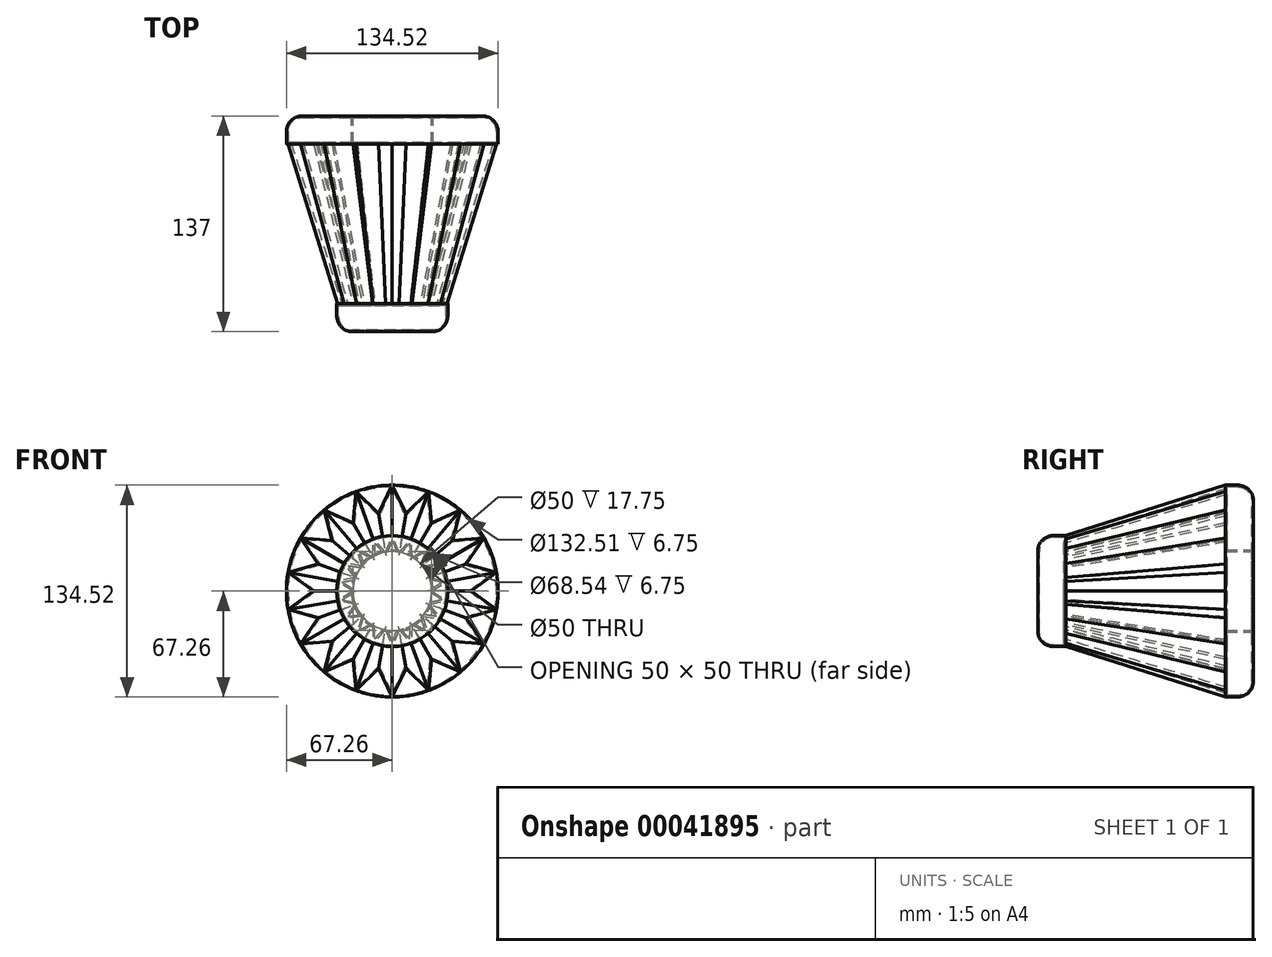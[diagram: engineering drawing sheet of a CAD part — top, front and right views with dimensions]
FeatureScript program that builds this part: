
annotation { "Feature Type Name" : "Feature", "Feature Type Description" : "" }
export const myFeature = defineFeature(function(context is Context, id is Id, definition is map)
    precondition{}
    {
        {
            var Q0;
            Q0=qCreatedBy(makeId("Front.planeOp"),FACE);
            var sketch = newSketch(context, id + "F0", { "sketchPlane" : qUnion([Q0])});
            skLineSegment(sketch, "E0", {"start": v(0, 0) * mm, "end": v(0, 67.26) * mm, "construction": true});
            skLineSegment(sketch, "E1", {"start": v(0, 0) * mm, "end": v(-8.68, 49.24) * mm});
            skLineSegment(sketch, "E2", {"start": v(-8.68, 49.24) * mm, "end": v(0, 67.26) * mm});
            skLineSegment(sketch, "E3.MirrorCS", {"start": v(8.68, 49.24) * mm, "end": v(0, 67.26) * mm});
            skLineSegment(sketch, "E4.MirrorCS", {"start": v(0, 0) * mm, "end": v(8.68, 49.24) * mm});
            skSolve(sketch);
        }
        {
            var Q0;
            Q0=qCreatedBy(makeId("Front.planeOp"),FACE);
            cPlane(context, id + "F1", {"entities" : qUnion([Q0]), "cplaneType" : CPlaneType.OFFSET, "offset" : 101.5 * mm, "width" : 150 * mm, "height" : 150 * mm});
        }
        {
            var Q0;
            Q0=qCreatedBy(id+"F1.planeOp",FACE);
            var sketch = newSketch(context, id + "F2", { "sketchPlane" : qUnion([Q0])});
            skLineSegment(sketch, "E5", {"start": v(0, 0) * mm, "end": v(0, 49.56) * mm, "construction": true});
            skLineSegment(sketch, "E6", {"start": v(0, 0) * mm, "end": v(-4.34, 24.62) * mm});
            skLineSegment(sketch, "E7", {"start": v(-4.34, 24.62) * mm, "end": v(0, 35.27) * mm});
            skLineSegment(sketch, "E8.MirrorCS", {"start": v(4.34, 24.62) * mm, "end": v(0, 35.27) * mm});
            skLineSegment(sketch, "E9.MirrorCS", {"start": v(0, 0) * mm, "end": v(4.34, 24.62) * mm});
            skSolve(sketch);
        }
        {
            var Q0;
            Q0=makeQuery(id+"F0.imprint","IMPRINT",FACE,{"disambiguationData":[TD([[makeQuery(id+"F0.imprint","IMPRINT",EDGE,{"derivedFrom":sQuery(id+"F0.wireOp",EDGE,"E1")}),-1.0]])]});
            var Q1;
            Q1=makeQuery(id+"F2.imprint","IMPRINT",FACE,{"disambiguationData":[TD([[makeQuery(id+"F2.imprint","IMPRINT",EDGE,{"derivedFrom":sQuery(id+"F2.wireOp",EDGE,"E6")}),-1.0]])]});
            loft(context, id + "F3", {"sheetProfilesArray" : [{ "sheetProfileEntities" : qUnion([Q0]) }, { "sheetProfileEntities" : qUnion([Q1]) }]});
        }
        {
            var Q0;
            Q0=makeQuery(id+"F3.opLoft","SWEPT_BODY",BODY,{"disambiguationData":[OSD([makeQuery(id+"F0.imprint","IMPRINT",FACE,{"disambiguationData":[TD([[makeQuery(id+"F0.imprint","IMPRINT",EDGE,{"derivedFrom":sQuery(id+"F0.wireOp",EDGE,"E1")}),-1.0]])]}),makeQuery(id+"F2.imprint","IMPRINT",FACE,{"disambiguationData":[TD([[makeQuery(id+"F2.imprint","IMPRINT",EDGE,{"derivedFrom":sQuery(id+"F2.wireOp",EDGE,"E6")}),-1.0]])]})])]});
            var Q1;
            Q1=makeQuery(id+"F3.opLoft","SWEPT_EDGE",EDGE,{"disambiguationData":[OSD([sQuery(id+"F0.wireOp",EDGE,"E1"),sQuery(id+"F0.wireOp",EDGE,"E4.MirrorCS"),sQuery(id+"F2.wireOp",EDGE,"E6"),sQuery(id+"F2.wireOp",EDGE,"E9.MirrorCS")])]});
            circularPattern(context, id + "F4", {"operationType" : NewBodyOperationType.ADD, "entities" : qUnion([Q0]), "axis" : qUnion([Q1]), "angle" : 360 * degree, "instanceCount" : 18, "equalSpace" : true});
        }
        {
            var Q0;
            {var subQ0=makeQuery(id+"F3.opLoft","CAP_FACE",FACE,{"disambiguationData":[OSD([makeQuery(id+"F2.imprint","IMPRINT",FACE,{"disambiguationData":[TD([[makeQuery(id+"F2.imprint","IMPRINT",EDGE,{"derivedFrom":sQuery(id+"F2.wireOp",EDGE,"E6")}),-1.0]])]})])],"isStart":true});Q0=makeQuery(id+"FTp9U8mSMzo62uv_1.opBoolean","MERGE",FACE,{"derivedFrom":[subQ0,makeQuery(id+"F4.opPattern","COPY",FACE,{"derivedFrom":subQ0,"instanceName":"1"}),makeQuery(id+"F4.opPattern","COPY",FACE,{"derivedFrom":subQ0,"instanceName":"2"}),makeQuery(id+"F4.opPattern","COPY",FACE,{"derivedFrom":subQ0,"instanceName":"3"}),makeQuery(id+"F4.opPattern","COPY",FACE,{"derivedFrom":subQ0,"instanceName":"4"}),makeQuery(id+"F4.opPattern","COPY",FACE,{"derivedFrom":subQ0,"instanceName":"5"}),makeQuery(id+"F4.opPattern","COPY",FACE,{"derivedFrom":subQ0,"instanceName":"6"}),makeQuery(id+"F4.opPattern","COPY",FACE,{"derivedFrom":subQ0,"instanceName":"7"}),makeQuery(id+"F4.opPattern","COPY",FACE,{"derivedFrom":subQ0,"instanceName":"8"}),makeQuery(id+"F4.opPattern","COPY",FACE,{"derivedFrom":subQ0,"instanceName":"9"}),makeQuery(id+"F4.opPattern","COPY",FACE,{"derivedFrom":subQ0,"instanceName":"10"}),makeQuery(id+"F4.opPattern","COPY",FACE,{"derivedFrom":subQ0,"instanceName":"11"}),makeQuery(id+"F4.opPattern","COPY",FACE,{"derivedFrom":subQ0,"instanceName":"12"}),makeQuery(id+"F4.opPattern","COPY",FACE,{"derivedFrom":subQ0,"instanceName":"13"}),makeQuery(id+"F4.opPattern","COPY",FACE,{"derivedFrom":subQ0,"instanceName":"14"}),makeQuery(id+"F4.opPattern","COPY",FACE,{"derivedFrom":subQ0,"instanceName":"15"}),makeQuery(id+"F4.opPattern","COPY",FACE,{"derivedFrom":subQ0,"instanceName":"16"}),makeQuery(id+"F4.opPattern","COPY",FACE,{"derivedFrom":subQ0,"instanceName":"17"})]});}
            var Q1;
            {var subQ0=makeQuery(id+"F3.opLoft","CAP_FACE",FACE,{"disambiguationData":[OSD([makeQuery(id+"F0.imprint","IMPRINT",FACE,{"disambiguationData":[TD([[makeQuery(id+"F0.imprint","IMPRINT",EDGE,{"derivedFrom":sQuery(id+"F0.wireOp",EDGE,"E1")}),-1.0]])]})])],"isStart":true});Q1=makeQuery(id+"FTp9U8mSMzo62uv_1.opBoolean","MERGE",FACE,{"derivedFrom":[subQ0,makeQuery(id+"F4.opPattern","COPY",FACE,{"derivedFrom":subQ0,"instanceName":"1"}),makeQuery(id+"F4.opPattern","COPY",FACE,{"derivedFrom":subQ0,"instanceName":"2"}),makeQuery(id+"F4.opPattern","COPY",FACE,{"derivedFrom":subQ0,"instanceName":"3"}),makeQuery(id+"F4.opPattern","COPY",FACE,{"derivedFrom":subQ0,"instanceName":"4"}),makeQuery(id+"F4.opPattern","COPY",FACE,{"derivedFrom":subQ0,"instanceName":"5"}),makeQuery(id+"F4.opPattern","COPY",FACE,{"derivedFrom":subQ0,"instanceName":"6"}),makeQuery(id+"F4.opPattern","COPY",FACE,{"derivedFrom":subQ0,"instanceName":"7"}),makeQuery(id+"F4.opPattern","COPY",FACE,{"derivedFrom":subQ0,"instanceName":"8"}),makeQuery(id+"F4.opPattern","COPY",FACE,{"derivedFrom":subQ0,"instanceName":"9"}),makeQuery(id+"F4.opPattern","COPY",FACE,{"derivedFrom":subQ0,"instanceName":"10"}),makeQuery(id+"F4.opPattern","COPY",FACE,{"derivedFrom":subQ0,"instanceName":"11"}),makeQuery(id+"F4.opPattern","COPY",FACE,{"derivedFrom":subQ0,"instanceName":"12"}),makeQuery(id+"F4.opPattern","COPY",FACE,{"derivedFrom":subQ0,"instanceName":"13"}),makeQuery(id+"F4.opPattern","COPY",FACE,{"derivedFrom":subQ0,"instanceName":"14"}),makeQuery(id+"F4.opPattern","COPY",FACE,{"derivedFrom":subQ0,"instanceName":"15"}),makeQuery(id+"F4.opPattern","COPY",FACE,{"derivedFrom":subQ0,"instanceName":"16"}),makeQuery(id+"F4.opPattern","COPY",FACE,{"derivedFrom":subQ0,"instanceName":"17"})]});}
            shell(context, id + "F5", {"entities" : qUnion([Q0, Q1]), "thickness" : 1 * mm});
        }
        {
            var Q0;
            Q0=qCreatedBy(makeId("Front.planeOp"),FACE);
            var sketch = newSketch(context, id + "F6", { "sketchPlane" : qUnion([Q0])});
            skCircle(sketch, "E10", {"center": v(0, 0) * mm, "radius": 67.26 * mm});
            skSolve(sketch);
        }
        {
            var Q0;
            Q0 = qSketchRegion(id + "F6", true);
            extrude(context, id + "F7", {"entities" : qUnion([Q0]), "oppositeDirection" : true, "depth" : 17.75 * mm});
        }
        {
            var Q0;
            Q0=qCreatedBy(id+"F1.planeOp",FACE);
            var sketch = newSketch(context, id + "F8", { "sketchPlane" : qUnion([Q0])});
            skCircle(sketch, "E11", {"center": v(0, 0) * mm, "radius": 35.27 * mm});
            skSolve(sketch);
        }
        {
            var Q0;
            Q0 = qSketchRegion(id + "F8", true);
            extrude(context, id + "F9", {"entities" : qUnion([Q0]), "depth" : 17.75 * mm});
        }
        {
            var Q0;
            Q0=makeQuery(id+"F9.opExtrude","CAP_EDGE",EDGE,{"disambiguationData":[OSD([sQuery(id+"F8.wireOp",EDGE,"E11")])],"isStart":false});
            var Q1;
            Q1=makeQuery(id+"F7.opExtrude","CAP_EDGE",EDGE,{"disambiguationData":[OSD([sQuery(id+"F6.wireOp",EDGE,"E10")])],"isStart":false});
            fillet(context, id + "F10", {"entities" : qUnion([Q0, Q1]), "radius" : 10 * mm, "tangentPropagation" : true, "allowEdgeOverflow" : false});
        }
        {
            var Q0;
            Q0=makeQuery(id+"F7.opExtrude","CAP_FACE",FACE,{"disambiguationData":[OSD([sQuery(id+"F6.wireOp",EDGE,"E10")])],"isStart":false});
            var sketch = newSketch(context, id + "F11", { "sketchPlane" : qUnion([Q0])});
            skCircle(sketch, "E12", {"center": v(0, 0) * mm, "radius": 25 * mm});
            skSolve(sketch);
        }
        {
            var Q0;
            Q0=makeQuery(id+"F11.imprint","IMPRINT",FACE,{"disambiguationData":[TD([[makeQuery(id+"F11.imprint","IMPRINT",EDGE,{"derivedFrom":sQuery(id+"F11.wireOp",EDGE,"E12")}),1.0]])]});
            extrude(context, id + "F12", {"entities" : qUnion([Q0]), "operationType" : NewBodyOperationType.REMOVE, "oppositeDirection" : true, "depth" : 17.8 * mm});
        }
    });
